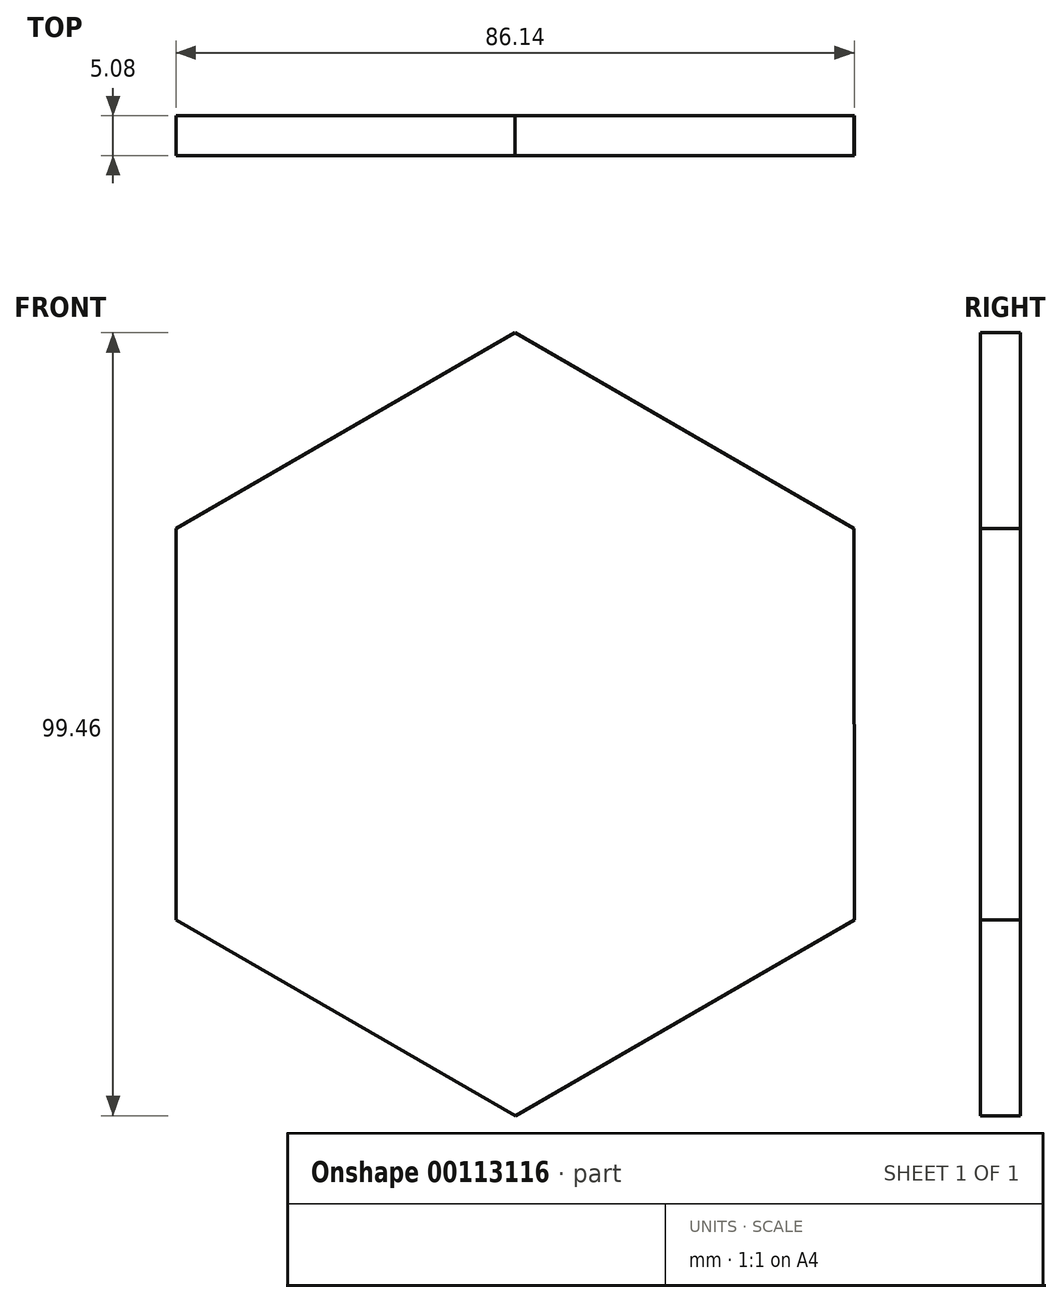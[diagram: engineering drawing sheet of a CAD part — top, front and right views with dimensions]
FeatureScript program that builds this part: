
annotation { "Feature Type Name" : "Feature", "Feature Type Description" : "" }
export const myFeature = defineFeature(function(context is Context, id is Id, definition is map)
    precondition{}
    {
        {
            var Q0;
            Q0=qCreatedBy(makeId("Front.planeOp"),FACE);
            var sketch = newSketch(context, id + "F0", { "sketchPlane" : qUnion([Q0])});
            skLineSegment(sketch, "E0.0", {"start": v(-43.07, 24.85) * mm, "end": v(-0.02, 49.73) * mm});
            skLineSegment(sketch, "E0.1", {"start": v(-0.02, 49.73) * mm, "end": v(43.06, 24.88) * mm});
            skLineSegment(sketch, "E0.2", {"start": v(43.06, 24.88) * mm, "end": v(43.07, -24.85) * mm});
            skLineSegment(sketch, "E0.3", {"start": v(43.07, -24.85) * mm, "end": v(0.02, -49.73) * mm});
            skLineSegment(sketch, "E0.4", {"start": v(0.02, -49.73) * mm, "end": v(-43.06, -24.88) * mm});
            skLineSegment(sketch, "E0.5", {"start": v(-43.06, -24.88) * mm, "end": v(-43.07, 24.85) * mm});
            skLineSegment(sketch, "E1", {"start": v(-43.07, 24.85) * mm, "end": v(0, 0) * mm});
            skLineSegment(sketch, "E2", {"start": v(0, 0) * mm, "end": v(-43.06, -24.88) * mm});
            skLineSegment(sketch, "E3", {"start": v(0.02, -49.73) * mm, "end": v(0, 0) * mm});
            skLineSegment(sketch, "E4", {"start": v(43.07, -24.85) * mm, "end": v(0, 0) * mm});
            skLineSegment(sketch, "E5", {"start": v(43.06, 24.88) * mm, "end": v(0, 0) * mm});
            skLineSegment(sketch, "E6", {"start": v(-0.02, 49.73) * mm, "end": v(0, 0) * mm});
            skSolve(sketch);
        }
        {
            var Q0;
            Q0=makeQuery(id+"F0.imprint","IMPRINT",FACE,{"disambiguationData":[TD([[makeQuery(id+"F0.imprint","IMPRINT",EDGE,{"derivedFrom":sQuery(id+"F0.wireOp",EDGE,"E0.0")}),-1.0]])]});
            var Q1;
            Q1=makeQuery(id+"F0.imprint","IMPRINT",FACE,{"disambiguationData":[TD([[makeQuery(id+"F0.imprint","IMPRINT",EDGE,{"derivedFrom":sQuery(id+"F0.wireOp",EDGE,"E0.5")}),-1.0]])]});
            var Q2;
            Q2=makeQuery(id+"F0.imprint","IMPRINT",FACE,{"disambiguationData":[TD([[makeQuery(id+"F0.imprint","IMPRINT",EDGE,{"derivedFrom":sQuery(id+"F0.wireOp",EDGE,"E0.4")}),-1.0]])]});
            var Q3;
            Q3=makeQuery(id+"F0.imprint","IMPRINT",FACE,{"disambiguationData":[TD([[makeQuery(id+"F0.imprint","IMPRINT",EDGE,{"derivedFrom":sQuery(id+"F0.wireOp",EDGE,"E0.3")}),-1.0]])]});
            var Q4;
            Q4=makeQuery(id+"F0.imprint","IMPRINT",FACE,{"disambiguationData":[TD([[makeQuery(id+"F0.imprint","IMPRINT",EDGE,{"derivedFrom":sQuery(id+"F0.wireOp",EDGE,"E0.2")}),-1.0]])]});
            var Q5;
            Q5=makeQuery(id+"F0.imprint","IMPRINT",FACE,{"disambiguationData":[TD([[makeQuery(id+"F0.imprint","IMPRINT",EDGE,{"derivedFrom":sQuery(id+"F0.wireOp",EDGE,"E0.1")}),-1.0]])]});
            extrude(context, id + "F1", {"entities" : qUnion([Q0, Q1, Q2, Q3, Q4, Q5]), "depth" : 5.08 * mm});
        }
    });
